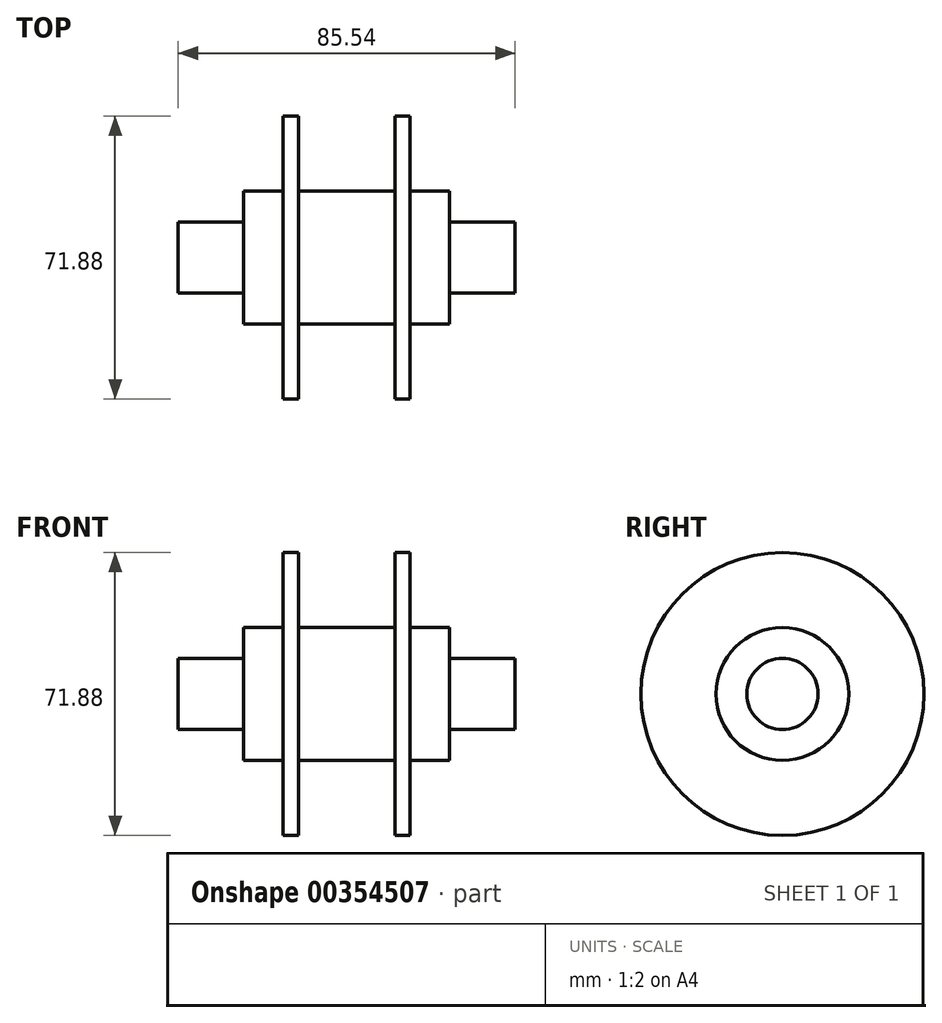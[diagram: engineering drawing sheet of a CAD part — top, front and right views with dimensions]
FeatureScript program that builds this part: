
annotation { "Feature Type Name" : "Feature", "Feature Type Description" : "" }
export const myFeature = defineFeature(function(context is Context, id is Id, definition is map)
    precondition{}
    {
        {
            var Q0;
            Q0=qCreatedBy(makeId("Front.planeOp"),FACE);
            var sketch = newSketch(context, id + "F0", { "sketchPlane" : qUnion([Q0])});
            skLineSegment(sketch, "E0.bottom", {"start": v(-42.77, 9.04) * mm, "end": v(-26.14, 9.04) * mm});
            skLineSegment(sketch, "E0.top", {"start": v(-42.77, 0) * mm, "end": v(0, 0) * mm});
            skLineSegment(sketch, "E0.left", {"start": v(-42.77, 9.04) * mm, "end": v(-42.77, 0) * mm});
            skLineSegment(sketch, "E0.right", {"start": v(0, 9.04) * mm, "end": v(0, 0) * mm});
            skLineSegment(sketch, "E1.left", {"start": v(0, 9.04) * mm, "end": v(0, 16.87) * mm});
            skLineSegment(sketch, "E1.right", {"start": v(-26.14, 9.04) * mm, "end": v(-26.14, 16.87) * mm});
            skLineSegment(sketch, "E2.top", {"start": v(-16.15, 35.94) * mm, "end": v(-12.24, 35.94) * mm});
            skLineSegment(sketch, "E2.left", {"start": v(-16.15, 16.87) * mm, "end": v(-16.15, 35.94) * mm});
            skLineSegment(sketch, "E2.right", {"start": v(-12.24, 16.87) * mm, "end": v(-12.24, 35.94) * mm});
            skLineSegment(sketch, "E3", {"start": v(-26.14, 16.87) * mm, "end": v(-16.15, 16.87) * mm});
            skLineSegment(sketch, "E4.trimOffspring", {"start": v(-12.24, 16.87) * mm, "end": v(0, 16.87) * mm});
            skSolve(sketch);
        }
        {
            var Q0;
            Q0 = qSketchRegion(id + "F0", true);
            var Q1;
            Q1=sQuery(id+"F0.wireOp",EDGE,"E0.top");
            revolve(context, id + "F1", {"entities" : qUnion([Q0]), "axis" : qUnion([Q1]), "revolveType" : RevolveType.FULL});
        }
        {
            var Q0;
            Q0=makeQuery(id+"F1.opRevolve","SWEPT_BODY",BODY,{"disambiguationData":[OSD([sQuery(id+"F0.wireOp",EDGE,"E0.bottom"),sQuery(id+"F0.wireOp",EDGE,"E0.top"),sQuery(id+"F0.wireOp",EDGE,"E0.left"),sQuery(id+"F0.wireOp",EDGE,"E0.right"),sQuery(id+"F0.wireOp",EDGE,"E1.left"),sQuery(id+"F0.wireOp",EDGE,"E1.right"),sQuery(id+"F0.wireOp",EDGE,"E2.top"),sQuery(id+"F0.wireOp",EDGE,"E2.left"),sQuery(id+"F0.wireOp",EDGE,"E2.right"),sQuery(id+"F0.wireOp",EDGE,"E3"),sQuery(id+"F0.wireOp",EDGE,"E4.trimOffspring")])]});
            var Q1;
            Q1=qCreatedBy(makeId("Right.planeOp"),FACE);
            mirror(context, id + "F2", {"operationType" : NewBodyOperationType.ADD, "entities" : qUnion([Q0]), "mirrorPlane" : qUnion([Q1])});
        }
    });
